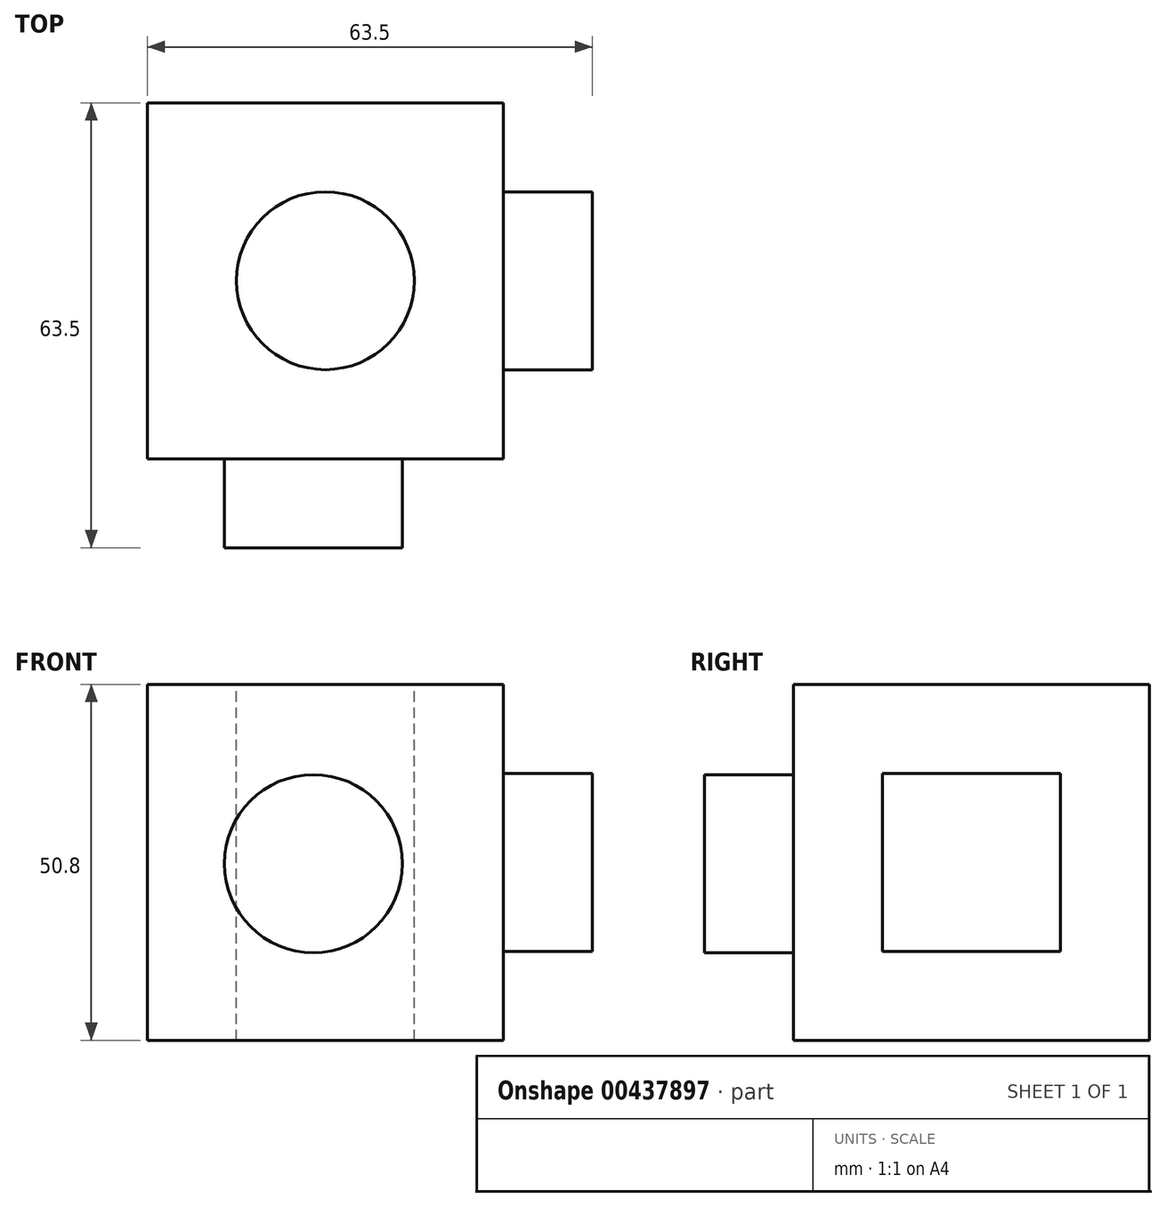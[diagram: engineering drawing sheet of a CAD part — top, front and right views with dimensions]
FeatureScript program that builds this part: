
annotation { "Feature Type Name" : "Feature", "Feature Type Description" : "" }
export const myFeature = defineFeature(function(context is Context, id is Id, definition is map)
    precondition{}
    {
        {
            var Q0;
            Q0=qCreatedBy(makeId("Front.planeOp"),FACE);
            var sketch = newSketch(context, id + "F0", { "sketchPlane" : qUnion([Q0])});
            skLineSegment(sketch, "E0.bottom", {"start": v(0, 0) * mm, "end": v(-50.8, 0) * mm});
            skLineSegment(sketch, "E0.top", {"start": v(0, 50.8) * mm, "end": v(-50.8, 50.8) * mm});
            skLineSegment(sketch, "E0.left", {"start": v(0, 0) * mm, "end": v(0, 50.8) * mm});
            skLineSegment(sketch, "E0.right", {"start": v(-50.8, 0) * mm, "end": v(-50.8, 50.8) * mm});
            skSolve(sketch);
        }
        {
            var Q0;
            Q0=makeQuery(id+"F0.imprint","IMPRINT",FACE,{"disambiguationData":[TD([[makeQuery(id+"F0.imprint","IMPRINT",EDGE,{"derivedFrom":sQuery(id+"F0.wireOp",EDGE,"E0.bottom")}),-1.0]])]});
            extrude(context, id + "F1", {"entities" : qUnion([Q0]), "depth" : 50.8 * mm});
        }
        {
            var Q0;
            Q0=makeQuery(id+"F1.opExtrude","CAP_FACE",FACE,{"disambiguationData":[OSD([sQuery(id+"F0.wireOp",EDGE,"E0.bottom"),sQuery(id+"F0.wireOp",EDGE,"E0.top"),sQuery(id+"F0.wireOp",EDGE,"E0.left"),sQuery(id+"F0.wireOp",EDGE,"E0.right")])],"isStart":false});
            var sketch = newSketch(context, id + "F2", { "sketchPlane" : qUnion([Q0])});
            skCircle(sketch, "E1", {"center": v(-27.12, 25.2) * mm, "radius": 12.7 * mm});
            skSolve(sketch);
        }
        {
            var Q0;
            Q0=makeQuery(id+"F2.imprint","IMPRINT",FACE,{"disambiguationData":[TD([[makeQuery(id+"F2.imprint","IMPRINT",EDGE,{"derivedFrom":sQuery(id+"F2.wireOp",EDGE,"E1")}),1.0]])]});
            extrude(context, id + "F3", {"entities" : qUnion([Q0]), "operationType" : NewBodyOperationType.ADD, "depth" : 12.7 * mm});
        }
        {
            var Q0;
            Q0=makeQuery(id+"F1.opExtrude","SWEPT_FACE",FACE,{"disambiguationData":[OSD([sQuery(id+"F0.wireOp",EDGE,"E0.left")])]});
            var sketch = newSketch(context, id + "F4", { "sketchPlane" : qUnion([Q0])});
            skLineSegment(sketch, "E2.bottom", {"start": v(-38.1, 38.1) * mm, "end": v(-12.7, 38.1) * mm});
            skLineSegment(sketch, "E2.top", {"start": v(-38.1, 12.7) * mm, "end": v(-12.7, 12.7) * mm});
            skLineSegment(sketch, "E2.left", {"start": v(-38.1, 38.1) * mm, "end": v(-38.1, 12.7) * mm});
            skLineSegment(sketch, "E2.right", {"start": v(-12.7, 38.1) * mm, "end": v(-12.7, 12.7) * mm});
            skPoint(sketch, "E2.middle", {"position": v(-25.4, 25.4) * mm});
            skPoint(sketch, "E2.middle.positionSnap0", {"position": v(0, 25.4) * mm});
            skPoint(sketch, "E2.middle.positionSnap1", {"position": v(-25.4, 50.8) * mm});
            skPoint(sketch, "E2.centerSnap0", {"position": v(0, 25.4) * mm});
            skPoint(sketch, "E2.centerSnap1", {"position": v(-25.4, 50.8) * mm});
            skSolve(sketch);
        }
        {
            var Q0;
            Q0=makeQuery(id+"F4.imprint","IMPRINT",FACE,{"disambiguationData":[TD([[makeQuery(id+"F4.imprint","IMPRINT",EDGE,{"derivedFrom":sQuery(id+"F4.wireOp",EDGE,"E2.bottom")}),-1.0]])]});
            extrude(context, id + "F5", {"entities" : qUnion([Q0]), "operationType" : NewBodyOperationType.ADD, "depth" : 12.7 * mm});
        }
        {
            var Q0;
            Q0=makeQuery(id+"F1.opExtrude","SWEPT_FACE",FACE,{"disambiguationData":[OSD([sQuery(id+"F0.wireOp",EDGE,"E0.top")])]});
            var sketch = newSketch(context, id + "F6", { "sketchPlane" : qUnion([Q0])});
            skCircle(sketch, "E3", {"center": v(-25.4, -25.4) * mm, "radius": 12.7 * mm});
            skPoint(sketch, "E3.centerSnap0", {"position": v(0, -25.4) * mm});
            skPoint(sketch, "E3.centerSnap1", {"position": v(-25.4, 0) * mm});
            skSolve(sketch);
        }
        {
            var Q0;
            Q0 = qSketchRegion(id + "F6", true);
            extrude(context, id + "F7", {"entities" : qUnion([Q0]), "operationType" : NewBodyOperationType.REMOVE, "oppositeDirection" : true, "depth" : 50.8 * mm});
        }
    });
